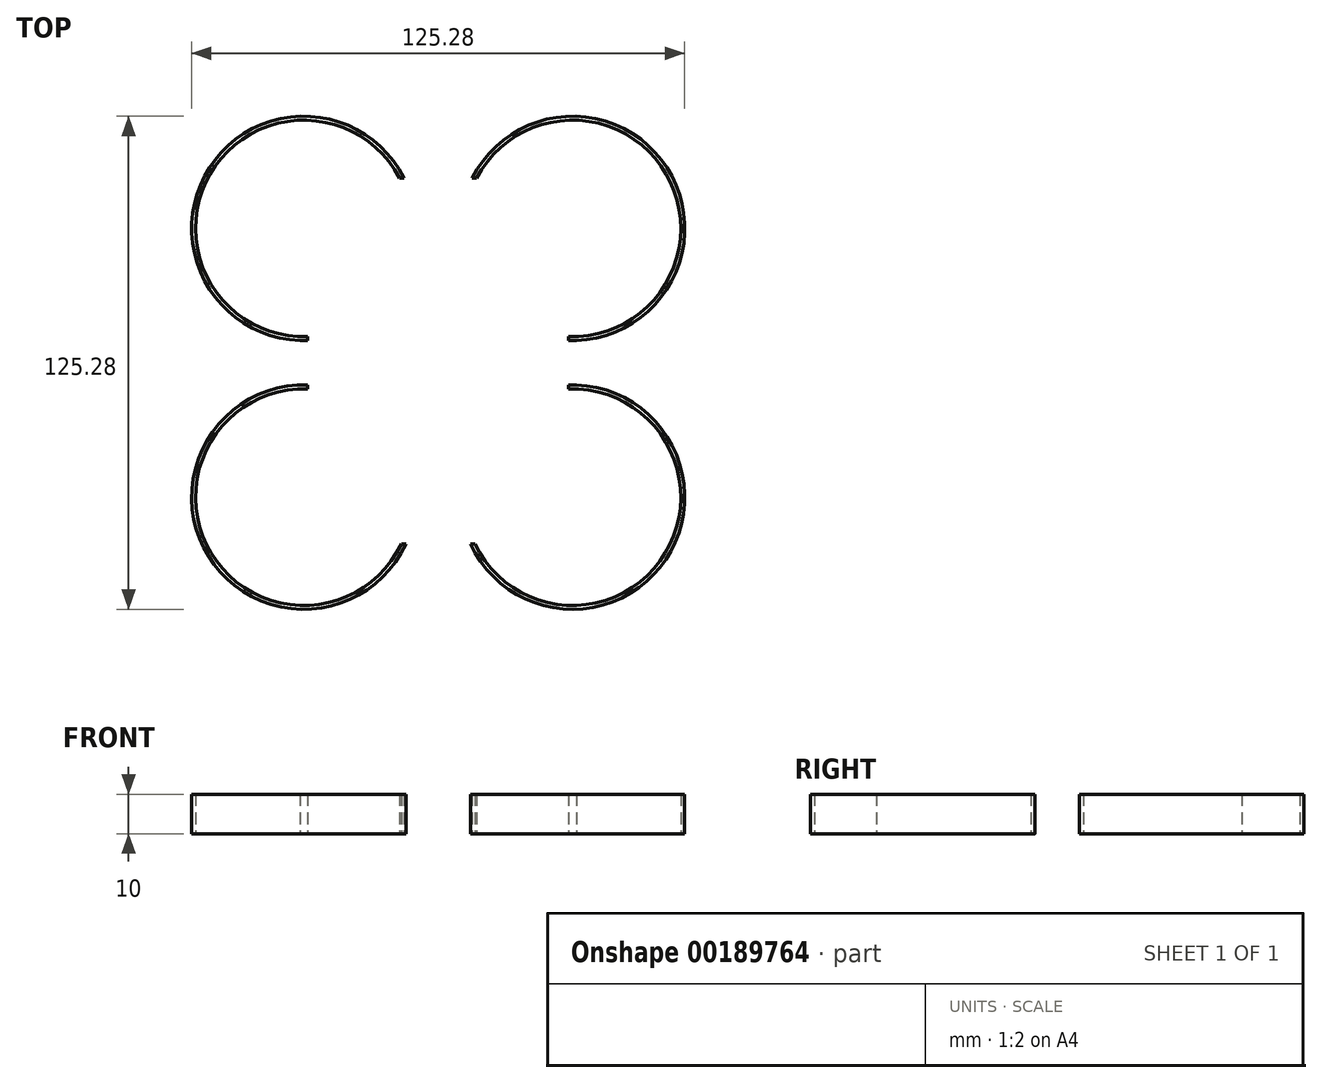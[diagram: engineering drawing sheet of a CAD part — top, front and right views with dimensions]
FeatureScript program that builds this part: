
annotation { "Feature Type Name" : "Feature", "Feature Type Description" : "" }
export const myFeature = defineFeature(function(context is Context, id is Id, definition is map)
    precondition{}
    {
        {
            var Q0;
            Q0=qCreatedBy(makeId("Top.planeOp"),FACE);
            var sketch = newSketch(context, id + "F0", { "sketchPlane" : qUnion([Q0])});
            skLineSegment(sketch, "E0", {"start": v(-34.14, 34.14) * mm, "end": v(0, 0) * mm, "construction": true});
            skLineSegment(sketch, "E1", {"start": v(0, 0) * mm, "end": v(-34.14, -34.14) * mm, "construction": true});
            skLineSegment(sketch, "E2", {"start": v(0, 0) * mm, "end": v(34.14, -34.14) * mm, "construction": true});
            skLineSegment(sketch, "E3", {"start": v(0, 0) * mm, "end": v(34.14, 34.14) * mm, "construction": true});
            skLineSegment(sketch, "E4", {"start": v(-69.73, 0) * mm, "end": v(71.64, 0) * mm, "construction": true});
            skCircle(sketch, "E5", {"center": v(-34.14, -34.14) * mm, "radius": 27.5 * mm});
            skCircle(sketch, "E6", {"center": v(34.14, -34.14) * mm, "radius": 27.5 * mm});
            skCircle(sketch, "E7", {"center": v(34.14, 34.14) * mm, "radius": 27.5 * mm});
            skCircle(sketch, "E8", {"center": v(-34.14, 34.14) * mm, "radius": 27.5 * mm});
            skCircle(sketch, "E9", {"center": v(-34.14, -34.14) * mm, "radius": 28.5 * mm});
            skCircle(sketch, "E10", {"center": v(-34.14, 34.14) * mm, "radius": 28.5 * mm});
            skCircle(sketch, "E11", {"center": v(34.14, 34.14) * mm, "radius": 28.5 * mm});
            skCircle(sketch, "E12", {"center": v(34.14, -34.14) * mm, "radius": 28.5 * mm});
            skLineSegment(sketch, "E13.bottom", {"start": v(16.5, -10) * mm, "end": v(-16.5, -10) * mm});
            skLineSegment(sketch, "E13.top", {"start": v(16.5, 10) * mm, "end": v(-16.5, 10) * mm});
            skLineSegment(sketch, "E13.left", {"start": v(16.5, -10) * mm, "end": v(16.5, 10) * mm});
            skLineSegment(sketch, "E13.right", {"start": v(-16.5, -10) * mm, "end": v(-16.5, 10) * mm});
            skPoint(sketch, "E13.middle", {"position": v(0, 0) * mm});
            skCircle(sketch, "E14", {"center": v(-34.14, -34.14) * mm, "radius": 3.5 * mm});
            skCircle(sketch, "E15", {"center": v(34.14, -34.14) * mm, "radius": 3.5 * mm});
            skCircle(sketch, "E16", {"center": v(34.14, 34.14) * mm, "radius": 3.5 * mm});
            skCircle(sketch, "E17", {"center": v(-34.14, 34.14) * mm, "radius": 3.5 * mm});
            skCircle(sketch, "E18", {"center": v(-34.14, -34.14) * mm, "radius": 6.5 * mm});
            skCircle(sketch, "E19", {"center": v(34.14, -34.14) * mm, "radius": 6.5 * mm});
            skCircle(sketch, "E20", {"center": v(34.14, 34.14) * mm, "radius": 6.5 * mm});
            skCircle(sketch, "E21", {"center": v(-34.14, 34.14) * mm, "radius": 6.5 * mm});
            skLineSegment(sketch, "E22.bottom", {"start": v(17.5, -11) * mm, "end": v(-17.5, -11) * mm});
            skLineSegment(sketch, "E22.top", {"start": v(17.5, 11) * mm, "end": v(-17.5, 11) * mm});
            skLineSegment(sketch, "E22.left", {"start": v(17.5, -11) * mm, "end": v(17.5, 11) * mm});
            skLineSegment(sketch, "E22.right", {"start": v(-17.5, -11) * mm, "end": v(-17.5, 11) * mm});
            skLineSegment(sketch, "E23", {"start": v(-34.14, 34.14) * mm, "end": v(-34.14, -34.14) * mm, "construction": true});
            skLineSegment(sketch, "E24", {"start": v(-34.14, -34.14) * mm, "end": v(34.14, -34.14) * mm, "construction": true});
            skLineSegment(sketch, "E25", {"start": v(34.14, -34.14) * mm, "end": v(34.14, 34.14) * mm, "construction": true});
            skLineSegment(sketch, "E26", {"start": v(34.14, 34.14) * mm, "end": v(-34.14, 34.14) * mm, "construction": true});
            skLineSegment(sketch, "E27", {"start": v(-35.14, 5.66) * mm, "end": v(-35.14, -5.66) * mm});
            skLineSegment(sketch, "E28", {"start": v(-33.14, 5.66) * mm, "end": v(-33.14, -5.66) * mm});
            skLineSegment(sketch, "E29", {"start": v(-35.14, -3.74) * mm, "end": v(-34.14, -3.74) * mm, "construction": true});
            skLineSegment(sketch, "E30", {"start": v(-33.14, -3.74) * mm, "end": v(-34.14, -3.74) * mm, "construction": true});
            skLineSegment(sketch, "E31", {"start": v(33.14, 5.66) * mm, "end": v(33.14, -5.66) * mm});
            skLineSegment(sketch, "E32", {"start": v(35.14, -5.66) * mm, "end": v(35.14, 5.66) * mm});
            skLineSegment(sketch, "E33", {"start": v(35.14, -8.8) * mm, "end": v(34.14, -8.8) * mm, "construction": true});
            skLineSegment(sketch, "E34", {"start": v(34.14, -8.8) * mm, "end": v(33.14, -8.8) * mm, "construction": true});
            skLineSegment(sketch, "E35", {"start": v(-5.66, 35.14) * mm, "end": v(5.66, 35.14) * mm});
            skLineSegment(sketch, "E36", {"start": v(5.66, 33.14) * mm, "end": v(-5.66, 33.14) * mm});
            skLineSegment(sketch, "E37", {"start": v(-3.76, 33.14) * mm, "end": v(-3.76, 34.14) * mm, "construction": true});
            skLineSegment(sketch, "E38", {"start": v(-3.76, 34.14) * mm, "end": v(-3.76, 35.14) * mm, "construction": true});
            skLineSegment(sketch, "E39", {"start": v(-5.66, -33.14) * mm, "end": v(5.66, -33.14) * mm});
            skLineSegment(sketch, "E40", {"start": v(-5.66, -35.14) * mm, "end": v(5.66, -35.14) * mm});
            skLineSegment(sketch, "E41", {"start": v(-0.9, -35.14) * mm, "end": v(-0.9, -34.14) * mm, "construction": true});
            skLineSegment(sketch, "E42", {"start": v(-0.9, -34.14) * mm, "end": v(-0.9, -33.14) * mm, "construction": true});
            skLineSegment(sketch, "E43", {"start": v(-34.14, 34.14) * mm, "end": v(-57.95, 47.89) * mm, "construction": true});
            skLineSegment(sketch, "E44", {"start": v(-34.14, 34.14) * mm, "end": v(-10.32, 47.89) * mm, "construction": true});
            skLineSegment(sketch, "E45", {"start": v(34.14, 34.14) * mm, "end": v(10.32, 47.89) * mm, "construction": true});
            skLineSegment(sketch, "E46", {"start": v(10.32, 47.89) * mm, "end": v(34.14, 34.14) * mm, "construction": true});
            skLineSegment(sketch, "E47", {"start": v(34.14, 34.14) * mm, "end": v(57.95, 47.89) * mm, "construction": true});
            skLineSegment(sketch, "E48", {"start": v(34.14, -34.14) * mm, "end": v(57.95, -47.89) * mm, "construction": true});
            skLineSegment(sketch, "E49", {"start": v(34.14, -34.14) * mm, "end": v(10.32, -47.89) * mm, "construction": true});
            skLineSegment(sketch, "E50", {"start": v(-34.14, -34.14) * mm, "end": v(-10.32, -47.89) * mm, "construction": true});
            skLineSegment(sketch, "E51", {"start": v(-34.14, -34.14) * mm, "end": v(-57.95, -47.89) * mm, "construction": true});
            skLineSegment(sketch, "E52.bottom", {"start": v(35.14, 5.66) * mm, "end": v(33.14, 5.66) * mm});
            skLineSegment(sketch, "E52.top", {"start": v(35.14, 33.92) * mm, "end": v(33.14, 33.92) * mm});
            skLineSegment(sketch, "E52.left", {"start": v(35.14, 5.66) * mm, "end": v(35.14, 33.92) * mm});
            skLineSegment(sketch, "E52.right", {"start": v(33.14, 5.66) * mm, "end": v(33.14, 33.92) * mm});
            skPoint(sketch, "E52.middle", {"position": v(34.14, 19.79) * mm});
            skLineSegment(sketch, "E53.bottom", {"start": v(35.14, -5.66) * mm, "end": v(33.14, -5.66) * mm});
            skLineSegment(sketch, "E53.top", {"start": v(35.14, -38.1) * mm, "end": v(33.14, -38.1) * mm});
            skLineSegment(sketch, "E53.left", {"start": v(35.14, -5.66) * mm, "end": v(35.14, -38.1) * mm});
            skLineSegment(sketch, "E53.right", {"start": v(33.14, -5.66) * mm, "end": v(33.14, -38.1) * mm});
            skPoint(sketch, "E53.middle", {"position": v(34.14, -21.88) * mm});
            skLineSegment(sketch, "E54.bottom", {"start": v(-33.14, -3.74) * mm, "end": v(-35.14, -3.74) * mm});
            skLineSegment(sketch, "E54.top", {"start": v(-33.14, -36.36) * mm, "end": v(-35.14, -36.36) * mm});
            skLineSegment(sketch, "E54.left", {"start": v(-33.14, -3.74) * mm, "end": v(-33.14, -36.36) * mm});
            skLineSegment(sketch, "E54.right", {"start": v(-35.14, -3.74) * mm, "end": v(-35.14, -36.36) * mm});
            skPoint(sketch, "E54.middle", {"position": v(-34.14, -20.05) * mm});
            skLineSegment(sketch, "E55.bottom", {"start": v(-33.14, 5.66) * mm, "end": v(-35.14, 5.66) * mm});
            skLineSegment(sketch, "E55.top", {"start": v(-33.14, 36.3) * mm, "end": v(-35.14, 36.3) * mm});
            skLineSegment(sketch, "E55.left", {"start": v(-33.14, 5.66) * mm, "end": v(-33.14, 36.3) * mm});
            skLineSegment(sketch, "E55.right", {"start": v(-35.14, 5.66) * mm, "end": v(-35.14, 36.3) * mm});
            skPoint(sketch, "E55.middle", {"position": v(-34.14, 20.98) * mm});
            skLineSegment(sketch, "E56", {"start": v(-10.32, -47.89) * mm, "end": v(10.32, -47.89) * mm, "construction": true});
            skLineSegment(sketch, "E57", {"start": v(-10.32, 47.89) * mm, "end": v(10.32, 47.89) * mm, "construction": true});
            skLineSegment(sketch, "E58.bottom", {"start": v(11.56, 46.89) * mm, "end": v(-11.56, 46.89) * mm});
            skLineSegment(sketch, "E58.top", {"start": v(11.56, 48.89) * mm, "end": v(-11.56, 48.89) * mm});
            skLineSegment(sketch, "E58.left", {"start": v(11.56, 46.89) * mm, "end": v(11.56, 48.89) * mm});
            skLineSegment(sketch, "E58.right", {"start": v(-11.56, 46.89) * mm, "end": v(-11.56, 48.89) * mm});
            skPoint(sketch, "E58.middle", {"position": v(0, 47.89) * mm});
            skLineSegment(sketch, "E59.bottom", {"start": v(10.32, -49.8) * mm, "end": v(-10.32, -49.8) * mm});
            skLineSegment(sketch, "E59.top", {"start": v(10.32, -45.98) * mm, "end": v(-10.32, -45.98) * mm});
            skLineSegment(sketch, "E59.left", {"start": v(10.32, -49.8) * mm, "end": v(10.32, -45.98) * mm});
            skLineSegment(sketch, "E59.right", {"start": v(-10.32, -49.8) * mm, "end": v(-10.32, -45.98) * mm});
            skPoint(sketch, "E59.middle", {"position": v(0, -47.89) * mm});
            skSolve(sketch);
        }
        {
            var Q0;
            Q0=makeQuery(id+"F0.imprint","IMPRINT",FACE,{"disambiguationData":[TD([[makeQuery(id+"F0.imprint","IMPRINT",EDGE,{"derivedFrom":sQuery(id+"F0.wireOp",EDGE,"E5")}),-1.0]])]});
            var Q1;
            Q1=makeQuery(id+"F0.imprint","IMPRINT",FACE,{"disambiguationData":[TD([[makeQuery(id+"F0.imprint","IMPRINT",EDGE,{"derivedFrom":sQuery(id+"F0.wireOp",EDGE,"E6")}),-1.0]])]});
            var Q2;
            Q2=makeQuery(id+"F0.imprint","IMPRINT",FACE,{"disambiguationData":[TD([[makeQuery(id+"F0.imprint","IMPRINT",EDGE,{"derivedFrom":sQuery(id+"F0.wireOp",EDGE,"E8")}),-1.0]])]});
            var Q3;
            Q3=makeQuery(id+"F0.imprint","IMPRINT",FACE,{"disambiguationData":[TD([[makeQuery(id+"F0.imprint","IMPRINT",EDGE,{"derivedFrom":sQuery(id+"F0.wireOp",EDGE,"E7")}),-1.0]])]});
            extrude(context, id + "F1", {"entities" : qUnion([Q0, Q1, Q2, Q3]), "depth" : 10 * mm});
        }
    });
